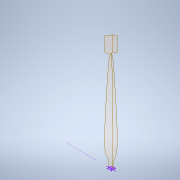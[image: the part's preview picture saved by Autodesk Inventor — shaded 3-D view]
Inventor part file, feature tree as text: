
AUTODESK INVENTOR PART (.ipt)
format: ipt  version: 2022 (Build 260153000, 153)  size: 850,944 bytes
history: native  units: mm
features: sketch x5, sweep x2, other x1
ambient origin geometry x8: Origin, YZ Plane, XZ Plane, XY Plane, X Axis, Y Axis, Z Axis, Center Point
bodies: Solid1 (feature_tree)
feature tree (8):
  sketch  "Sketch1"  dims[d0=380.0mm d1=90.0deg]
  sketch  "Sketch2"  dims[d8=330.0mm d9=90.0deg]
  sketch  "3D Sketch1"
  sweep  "Sweep2"
  sketch  "Sketch3"  dims[d10=0.0mm d11=0.0mm d12=0.0mm d13=0.0mm]
  sketch  "3D Sketch2"
  other  "Srf1"
  sweep  "SweepSrf1"
